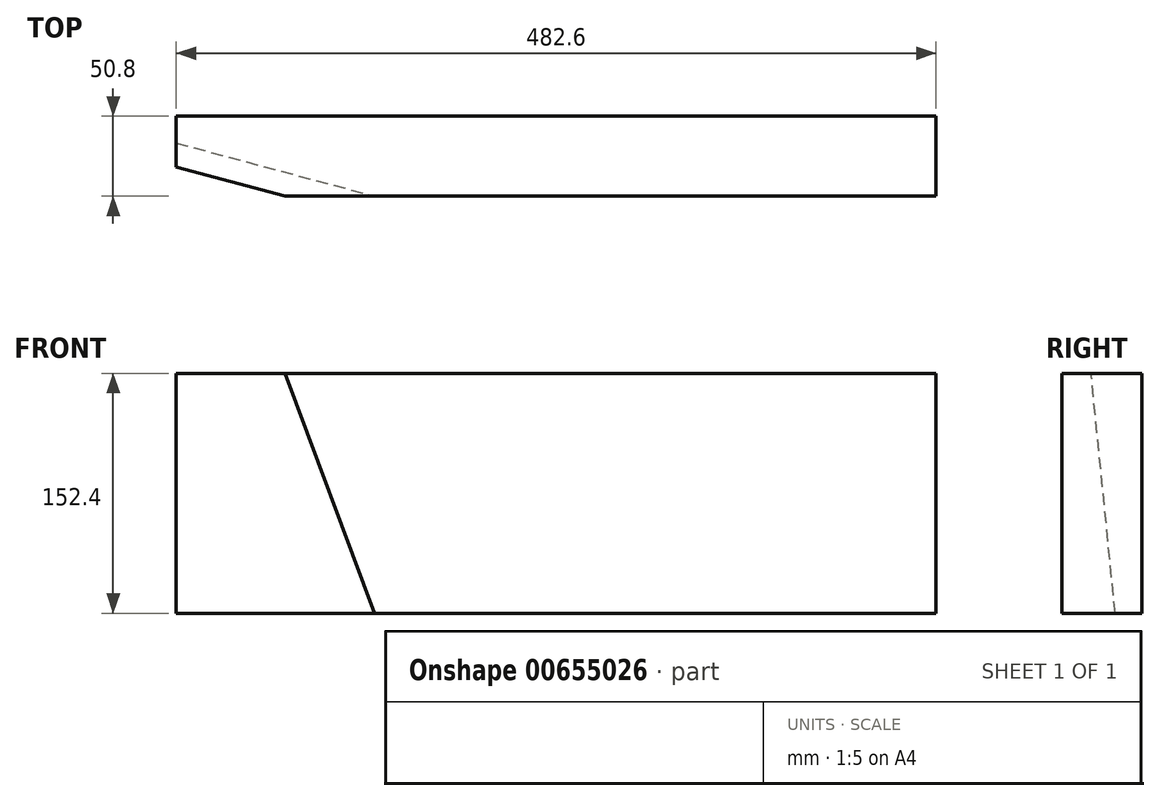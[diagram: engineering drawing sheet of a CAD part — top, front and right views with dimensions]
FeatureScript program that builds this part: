
annotation { "Feature Type Name" : "Feature", "Feature Type Description" : "" }
export const myFeature = defineFeature(function(context is Context, id is Id, definition is map)
    precondition{}
    {
        {
            var Q0;
            Q0=qCreatedBy(makeId("Top.planeOp"),FACE);
            var sketch = newSketch(context, id + "F0", { "sketchPlane" : qUnion([Q0])});
            skLineSegment(sketch, "E0.bottom", {"start": v(-241.3, 25.4) * mm, "end": v(241.3, 25.4) * mm});
            skLineSegment(sketch, "E0.top", {"start": v(-241.3, -25.4) * mm, "end": v(241.3, -25.4) * mm});
            skLineSegment(sketch, "E0.left", {"start": v(-241.3, 25.4) * mm, "end": v(-241.3, -25.4) * mm});
            skLineSegment(sketch, "E0.right", {"start": v(241.3, 25.4) * mm, "end": v(241.3, -25.4) * mm});
            skLineSegment(sketch, "E1", {"start": v(0, 0) * mm, "end": v(0, -25.4) * mm, "construction": true});
            skSolve(sketch);
        }
        {
            var Q0;
            Q0 = qSketchRegion(id + "F0", true);
            extrude(context, id + "F1", {"entities" : qUnion([Q0]), "depth" : 152.4 * mm, "offsetDistance" : 25.4 * mm});
        }
        {
            var Q0;
            Q0=makeQuery(id+"F1.opExtrude","CAP_FACE",FACE,{"disambiguationData":[OSD([sQuery(id+"F0.wireOp",EDGE,"E0.bottom"),sQuery(id+"F0.wireOp",EDGE,"E0.top"),sQuery(id+"F0.wireOp",EDGE,"E0.left"),sQuery(id+"F0.wireOp",EDGE,"E0.right")])],"isStart":true});
            var sketch = newSketch(context, id + "F2", { "sketchPlane" : qUnion([Q0])});
            skLineSegment(sketch, "E2", {"start": v(-241.3, -8.38) * mm, "end": v(-115.22, 25.4) * mm});
            skLineSegment(sketch, "E3", {"start": v(-115.22, 25.4) * mm, "end": v(-241.3, 25.4) * mm});
            skLineSegment(sketch, "E4", {"start": v(-241.3, 25.4) * mm, "end": v(-241.3, -8.38) * mm});
            skSolve(sketch);
        }
        {
            var Q0;
            Q0=makeQuery(id+"F1.opExtrude","SWEPT_FACE",FACE,{"disambiguationData":[OSD([sQuery(id+"F0.wireOp",EDGE,"E0.left")])]});
            var sketch = newSketch(context, id + "F3", { "sketchPlane" : qUnion([Q0])});
            skLineSegment(sketch, "E5", {"start": v(15.94, 242.24) * mm, "end": v(-8.38, 0) * mm});
            skSolve(sketch);
        }
        {
            var Q0;
            Q0 = qSketchRegion(id + "F2", true);
            var Q1;
            Q1 = qConstructionFilter(qBodyType(qCreatedBy(id + "F3" ,EDGE), BodyType.WIRE), ConstructionObject.NO);
            sweep(context, id + "F4", {"operationType" : NewBodyOperationType.REMOVE, "profiles" : qUnion([Q0]), "path" : qUnion([Q1])});
        }
    });
